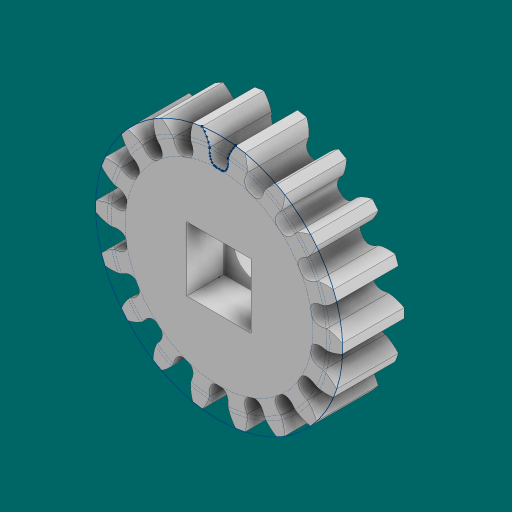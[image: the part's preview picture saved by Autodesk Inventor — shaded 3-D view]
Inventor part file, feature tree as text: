
AUTODESK INVENTOR PART (.ipt)
format: ipt  version: 2023.1 (Build 271208000, 208)  size: 317,440 bytes
history: native  units: in
note: dims shown in document units (in); Inventor stores cm internally (conversion verified against a paired STEP export)
features: extrude x5, sketch x4, pattern_circular x1, chamfer x1
ambient origin geometry x8: Origin, YZ Plane, XZ Plane, XY Plane, X Axis, Y Axis, Z Axis, Center Point
bodies: Solid1 (feature_tree)
feature tree (11):
  sketch  "Sketch1"  dims[d0=0.25in d1=0.0in]
  extrude  "Extrusion1"  TaperAngle=0.0deg  [1 undecoded]
  extrude  "Extrusion2"  Depth=7.0866in TaperAngle=360.0deg
  pattern_circular  "Circular Pattern1"  [2 undecoded]
  extrude  "Extrusion3"  Depth=0.05in TaperAngle=0.0deg
  extrude  "Extrusion4"  Depth=0.05in TaperAngle=0.0deg
  extrude  "Extrusion5"  Depth=0.05in TaperAngle=45.0deg
  chamfer  "Chamfer1"  Distance=0.18in
  sketch  "Sketch2"  dims[d2=0.0in d3=0.0in d4=7.0866in d5=360.0deg]
  sketch  "Sketch3"  dims[d9=0.0in d10=0.0in]
  sketch  "Sketch4"  dims[d11=0.26in d12=0.26in d13=0.15in d14=0.0in d16=0.05in d17=0.0in d18=0.0118in d19=0.125in d20=45.0deg d21=0.18in d22=0.18in d23=0.33in]
note: 3 required parameter values undecoded (feature->parameter linkage not recoverable at this tier; creation-order binding heuristic only, values carry confidence <= 0.55)
